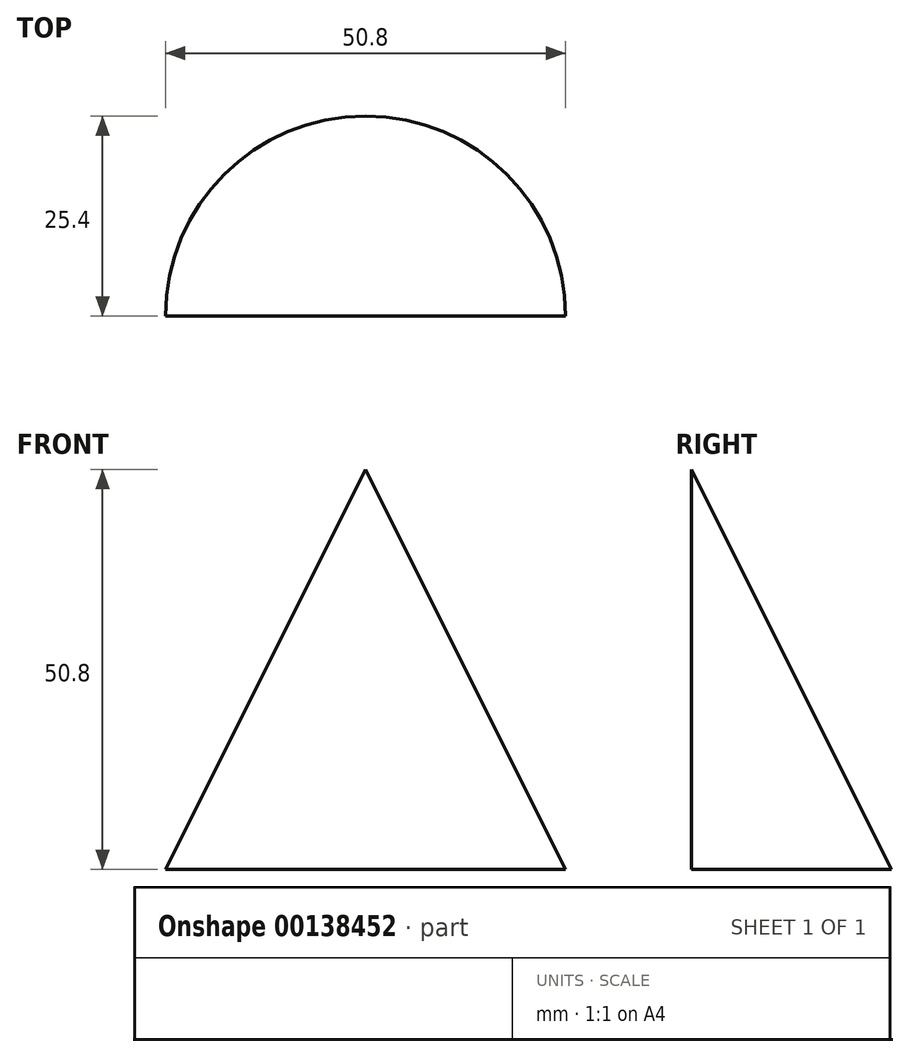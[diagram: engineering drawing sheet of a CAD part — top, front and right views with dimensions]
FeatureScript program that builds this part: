
annotation { "Feature Type Name" : "Feature", "Feature Type Description" : "" }
export const myFeature = defineFeature(function(context is Context, id is Id, definition is map)
    precondition{}
    {
        {
            var Q0;
            Q0=qCreatedBy(makeId("Top.planeOp"),FACE);
            var sketch = newSketch(context, id + "F0", { "sketchPlane" : qUnion([Q0])});
            skCircle(sketch, "E0", {"center": v(0, 0) * mm, "radius": 25.4 * mm});
            skSolve(sketch);
        }
        {
            var Q0;
            Q0 = qSketchRegion(id + "F0", true);
            extrude(context, id + "F1", {"entities" : qUnion([Q0]), "depth" : 50.8 * mm});
        }
        {
            var Q0;
            Q0=makeQuery(id+"F1.opExtrude","CAP_EDGE",EDGE,{"disambiguationData":[OSD([sQuery(id+"F0.wireOp",EDGE,"E0")])],"isStart":false});
            chamfer(context, id + "F2", {"entities" : qUnion([Q0]), "chamferType" : ChamferType.TWO_OFFSETS, "width1" : 25.4 * mm, "oppositeDirection" : false, "width2" : 50.8 * mm, "tangentPropagation" : true});
        }
        {
            var Q0;
            Q0=makeQuery(id+"F1.opExtrude","CAP_FACE",FACE,{"disambiguationData":[OSD([sQuery(id+"F0.wireOp",EDGE,"E0")])],"isStart":true});
            var sketch = newSketch(context, id + "F3", { "sketchPlane" : qUnion([Q0])});
            skLineSegment(sketch, "E1.bottom", {"start": v(-25.4, 0) * mm, "end": v(25.4, 0) * mm});
            skLineSegment(sketch, "E1.top", {"start": v(-25.4, 25.4) * mm, "end": v(25.4, 25.4) * mm});
            skLineSegment(sketch, "E1.left", {"start": v(-25.4, 0) * mm, "end": v(-25.4, 25.4) * mm});
            skLineSegment(sketch, "E1.right", {"start": v(25.4, 0) * mm, "end": v(25.4, 25.4) * mm});
            skSolve(sketch);
        }
        {
            var Q0;
            Q0 = qSketchRegion(id + "F3", true);
            var Q1;
            Q1=makeQuery(id+"F2.opChamfer","BLEND_FACE",FACE,{"disambiguationData":[OSD([sQuery(id+"F0.wireOp",EDGE,"E0")])]});
            extrude(context, id + "F4", {"entities" : qUnion([Q0]), "operationType" : NewBodyOperationType.REMOVE, "endBound" : BoundingType.UP_TO_SURFACE, "oppositeDirection" : true, "endBoundEntityFace" : qUnion([Q1]), "depth" : 25.4 * mm});
        }
    });
